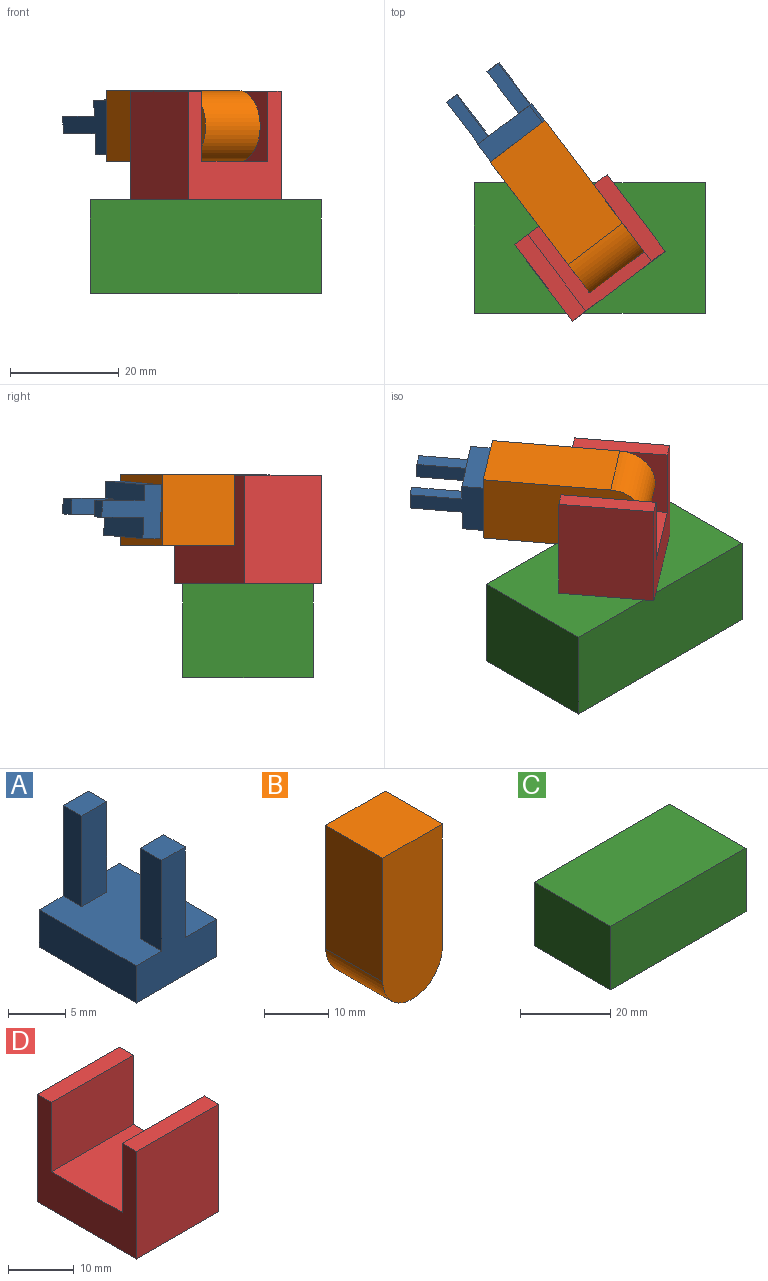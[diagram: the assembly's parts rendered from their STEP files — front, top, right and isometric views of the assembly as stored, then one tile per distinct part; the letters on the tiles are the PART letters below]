
ASSEMBLY  parts=4 mates=4
PART A: 14 faces, bbox 9.9x11.9x13.6 mm
  f0: plane 11.94x3.97mm, normal (-1,0,0), area 47.3mm2, adj f1,f3,f4,f5
  f1: plane 11.94x9.93mm, normal (0,0,1), area 103.9mm2, adj f0,f2,f4,f5,f6,f7,f8,f10
  f2: plane 11.94x3.97mm, normal (1,0,0), area 47.3mm2, adj f1,f3,f4,f5
  f3: plane 11.94x9.93mm, normal (0,0,-1), area 118.5mm2, adj f0,f2,f4,f5
  f4: plane 13.62x9.93mm, normal (0,1,0), area 69.1mm2, adj f0,f1,f2,f3,f10,f12,f13
  f5: plane 13.62x9.93mm, normal (0,-1,0), area 67.3mm2, adj f0,f1,f2,f3,f6,f7,f9
  f6: plane 9.65x2.63mm, normal (-1,0,0), area 25.3mm2, adj f1,f5,f8,f9
  f7: plane 9.65x2.63mm, normal (1,0,0), area 25.3mm2, adj f1,f5,f8,f9
  f8: plane 9.65x2.89mm, normal (0,1,0), area 27.9mm2, adj f1,f6,f7,f9
  f9: plane 2.89x2.63mm, normal (0,0,1), area 7.6mm2, adj f5,f6,f7,f8
  f10: plane 9.65x2.28mm, normal (-1,0,0), area 22mm2, adj f1,f4,f11,f13
  f11: plane 9.65x3.08mm, normal (0,-1,0), area 29.8mm2, adj f1,f10,f12,f13
  f12: plane 9.65x2.28mm, normal (1,0,0), area 22mm2, adj f1,f4,f11,f13
  f13: plane 3.08x2.28mm, normal (0,0,1), area 7mm2, adj f4,f10,f11,f12
PART B: 6 faces, bbox 13.1x12.6x30.2 mm
  f0: cylinder r=6.56mm len=13.11mm, axis (0,-1,0), area 259.5mm2, adj f1,f3,f4,f5
  f1: plane 23.65x12.6mm, normal (-1,0,0), area 298mm2, adj f0,f2,f4,f5
  f2: plane 13.11x12.6mm, normal (0,0,1), area 165.2mm2, adj f1,f3,f4,f5
  f3: plane 23.65x12.6mm, normal (1,0,0), area 298mm2, adj f0,f2,f4,f5
  f4: plane 30.21x13.11mm, normal (0,1,0), area 377.7mm2, adj f0,f1,f2,f3
  f5: plane 30.21x13.11mm, normal (0,-1,0), area 377.7mm2, adj f0,f1,f2,f3
PART C: 6 faces, bbox 42.5x24x17.3 mm
  f0: plane 24x17.27mm, normal (-1,0,0), area 414.5mm2, adj f1,f3,f4,f5
  f1: plane 42.49x17.27mm, normal (0,-1,0), area 733.8mm2, adj f0,f2,f4,f5
  f2: plane 24x17.27mm, normal (1,0,0), area 414.5mm2, adj f1,f3,f4,f5
  f3: plane 42.49x17.27mm, normal (0,1,0), area 733.8mm2, adj f0,f2,f4,f5
  f4: plane 42.49x24mm, normal (0,0,1), area 1019.6mm2, adj f0,f1,f2,f3
  f5: plane 42.49x24mm, normal (0,0,-1), area 1019.6mm2, adj f0,f1,f2,f3
PART D: 10 faces, bbox 17.7x21.4x20 mm
  f0: plane 17.66x15.19mm, normal (0,0,1), area 268.2mm2, adj f1,f3,f6,f8
  f1: plane 21.36x20.02mm, normal (-1,0,0), area 231.7mm2, adj f0,f2,f4,f5,f6,f7,f8,f9
  f2: plane 20.02x17.66mm, normal (0,-1,0), area 353.5mm2, adj f1,f3,f5,f7
  f3: plane 21.36x20.02mm, normal (1,0,0), area 231.7mm2, adj f0,f2,f4,f5,f6,f7,f8,f9
  f4: plane 20.02x17.66mm, normal (0,1,0), area 353.5mm2, adj f1,f3,f5,f9
  f5: plane 21.36x17.66mm, normal (0,0,-1), area 377.3mm2, adj f1,f2,f3,f4
  f6: plane 17.66x12.9mm, normal (0,1,0), area 227.9mm2, adj f0,f1,f3,f7
  f7: plane 17.66x3.12mm, normal (0,0,1), area 55.2mm2, adj f1,f2,f3,f6
  f8: plane 17.66x12.9mm, normal (0,-1,0), area 227.9mm2, adj f0,f1,f3,f9
  f9: plane 17.66x3.06mm, normal (0,0,1), area 53.9mm2, adj f1,f3,f4,f8
PLACE A rot(axis=(-0.68,0.31,0.66),141.2deg) t=(31.58,-27.9,15.53)mm
PLACE B rot(axis=(-0.67,0.33,0.67),143.3deg) t=(38.09,-34.56,15.05)mm
PLACE C t=(-21.21,-18.31,-36.67)mm fixed
PLACE D rot(axis=(0,0,1),127.2deg) t=(22.43,-15.99,-36.67)mm
MATE revolute C.f4 <-> D.f5  axis (0,0,1) through (0.04,-6.31,-19.39)mm
MATE planar B.f2 <-> A.f3  axis (-0.6,0.8,0) through (-13.25,13.31,-5.8)mm
MATE cylindrical A.f3 <-> B.f2  axis (0.6,-0.8,0) through (-13.25,13.31,-5.8)mm
MATE revolute D.f6 <-> B.f0  axis (-0.8,-0.6,0) through (6.06,-1.74,-5.83)mm
